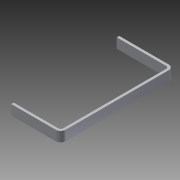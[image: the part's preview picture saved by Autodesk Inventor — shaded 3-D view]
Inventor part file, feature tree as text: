
AUTODESK INVENTOR PART (.ipt)
format: ipt  version: 2013 (Build 170138000, 138)  size: 107,008 bytes
history: native  units: in
note: dims shown in document units (in); Inventor stores cm internally (conversion verified against a paired STEP export)
features: sheet_metal_op x7, other x3, sketch x2
ambient origin geometry x8: Origin, YZ Plane, XZ Plane, XY Plane, X Axis, Y Axis, Z Axis, Center Point
feature tree (12):
  sheet_metal_op  "Face2"
  sheet_metal_op  "Flange4"
  sheet_metal_op  "Flange5"
  other  "Plate5"
  sketch  "Sketch6"  dims[d1=2.244in]
  other  "Plate6"
  sheet_metal_op  "Bend4"
  sheet_metal_op  "Corner4"
  sketch  "Sketch7"  dims[d2=0.5in d5=0.295in d8=0.125in d42=0.125in d43=0.125in d44=0.0625in d45=0.25in d46=0.125in d47=5.447in d48=90.0deg d49=0.125in d50=0.5in d51=0.125in d52=0.125in d53=0.125in d54=0.0625in d55=0.25in d56=0.125in d57=2.744in d58=90.0deg d59=0.125in d60=0.5in d61=0.125in d62=0.125in]
  other  "Plate7"
  sheet_metal_op  "Bend5"
  sheet_metal_op  "Corner5"
